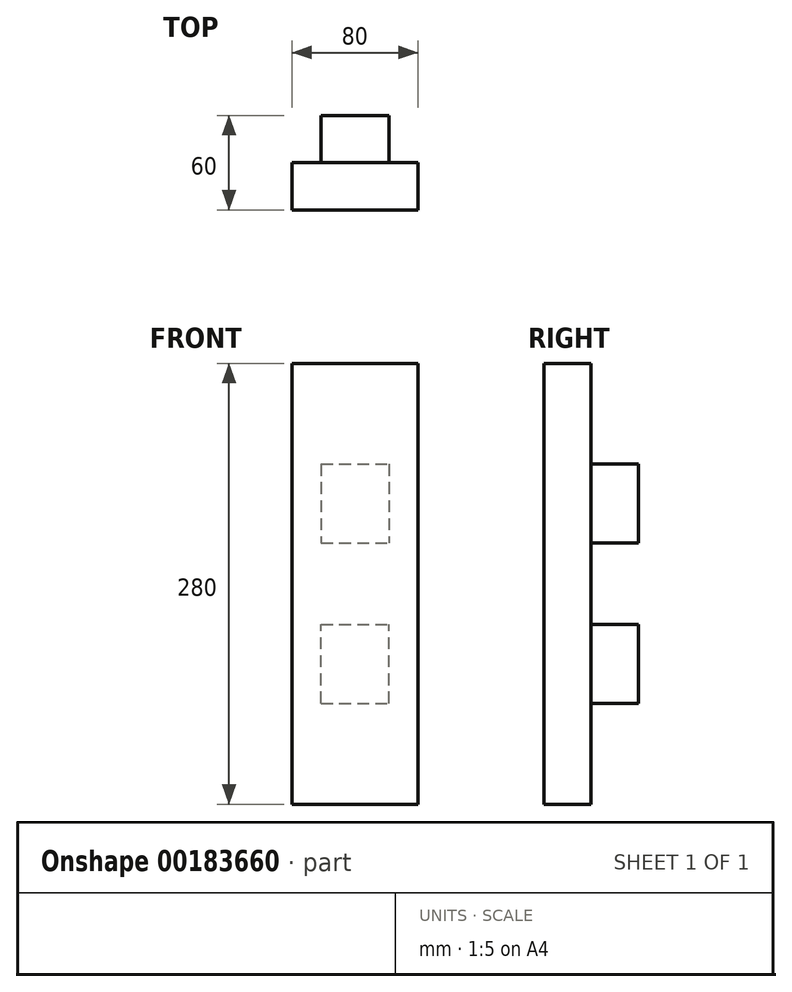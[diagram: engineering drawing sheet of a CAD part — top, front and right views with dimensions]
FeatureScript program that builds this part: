
annotation { "Feature Type Name" : "Feature", "Feature Type Description" : "" }
export const myFeature = defineFeature(function(context is Context, id is Id, definition is map)
    precondition{}
    {
        {
            var Q0;
            Q0=qCreatedBy(makeId("Front.planeOp"),FACE);
            var sketch = newSketch(context, id + "F0", { "sketchPlane" : qUnion([Q0])});
            skLineSegment(sketch, "E0.bottom", {"start": v(40, -140) * mm, "end": v(-40, -140) * mm});
            skLineSegment(sketch, "E0.top", {"start": v(40, 140) * mm, "end": v(-40, 140) * mm});
            skLineSegment(sketch, "E0.left", {"start": v(40, -140) * mm, "end": v(40, 140) * mm});
            skLineSegment(sketch, "E0.right", {"start": v(-40, -140) * mm, "end": v(-40, 140) * mm});
            skPoint(sketch, "E0.middle", {"position": v(0, 0) * mm});
            skSolve(sketch);
        }
        {
            var Q0;
            Q0=makeQuery(id+"F0.imprint","IMPRINT",FACE,{"disambiguationData":[TD([[makeQuery(id+"F0.imprint","IMPRINT",EDGE,{"derivedFrom":sQuery(id+"F0.wireOp",EDGE,"E0.bottom")}),-1.0]])]});
            extrude(context, id + "F1", {"entities" : qUnion([Q0]), "depth" : 30 * mm});
        }
        {
            var Q0;
            Q0=qCreatedBy(makeId("Top.planeOp"),FACE);
            var sketch = newSketch(context, id + "F2", { "sketchPlane" : qUnion([Q0])});
            skLineSegment(sketch, "E1.bottom", {"start": v(-21.5, 0) * mm, "end": v(21.5, 0) * mm});
            skLineSegment(sketch, "E1.top", {"start": v(-21.5, 30) * mm, "end": v(21.5, 30) * mm});
            skLineSegment(sketch, "E1.left", {"start": v(-21.5, 0) * mm, "end": v(-21.5, 30) * mm});
            skLineSegment(sketch, "E1.right", {"start": v(21.5, 0) * mm, "end": v(21.5, 30) * mm});
            skSolve(sketch);
        }
        {
            var Q0;
            Q0=makeQuery(id+"F2.imprint","IMPRINT",FACE,{"disambiguationData":[TD([[makeQuery(id+"F2.imprint","IMPRINT",EDGE,{"derivedFrom":sQuery(id+"F2.wireOp",EDGE,"E1.bottom")}),1.0]])]});
            extrude(context, id + "F3", {"entities" : qUnion([Q0]), "operationType" : NewBodyOperationType.ADD, "depth" : 76 * mm, "hasSecondDirection" : true, "secondDirectionOppositeDirection" : false, "secondDirectionDepth" : 26 * mm});
        }
        {
            var Q0;
            Q0=makeQuery(id+"F2.imprint","IMPRINT",FACE,{"disambiguationData":[TD([[makeQuery(id+"F2.imprint","IMPRINT",EDGE,{"derivedFrom":sQuery(id+"F2.wireOp",EDGE,"E1.bottom")}),1.0]])]});
            extrude(context, id + "F4", {"entities" : qUnion([Q0]), "operationType" : NewBodyOperationType.ADD, "oppositeDirection" : true, "depth" : 76 * mm, "hasSecondDirection" : true, "secondDirectionOppositeDirection" : true, "secondDirectionDepth" : 26 * mm});
        }
    });
